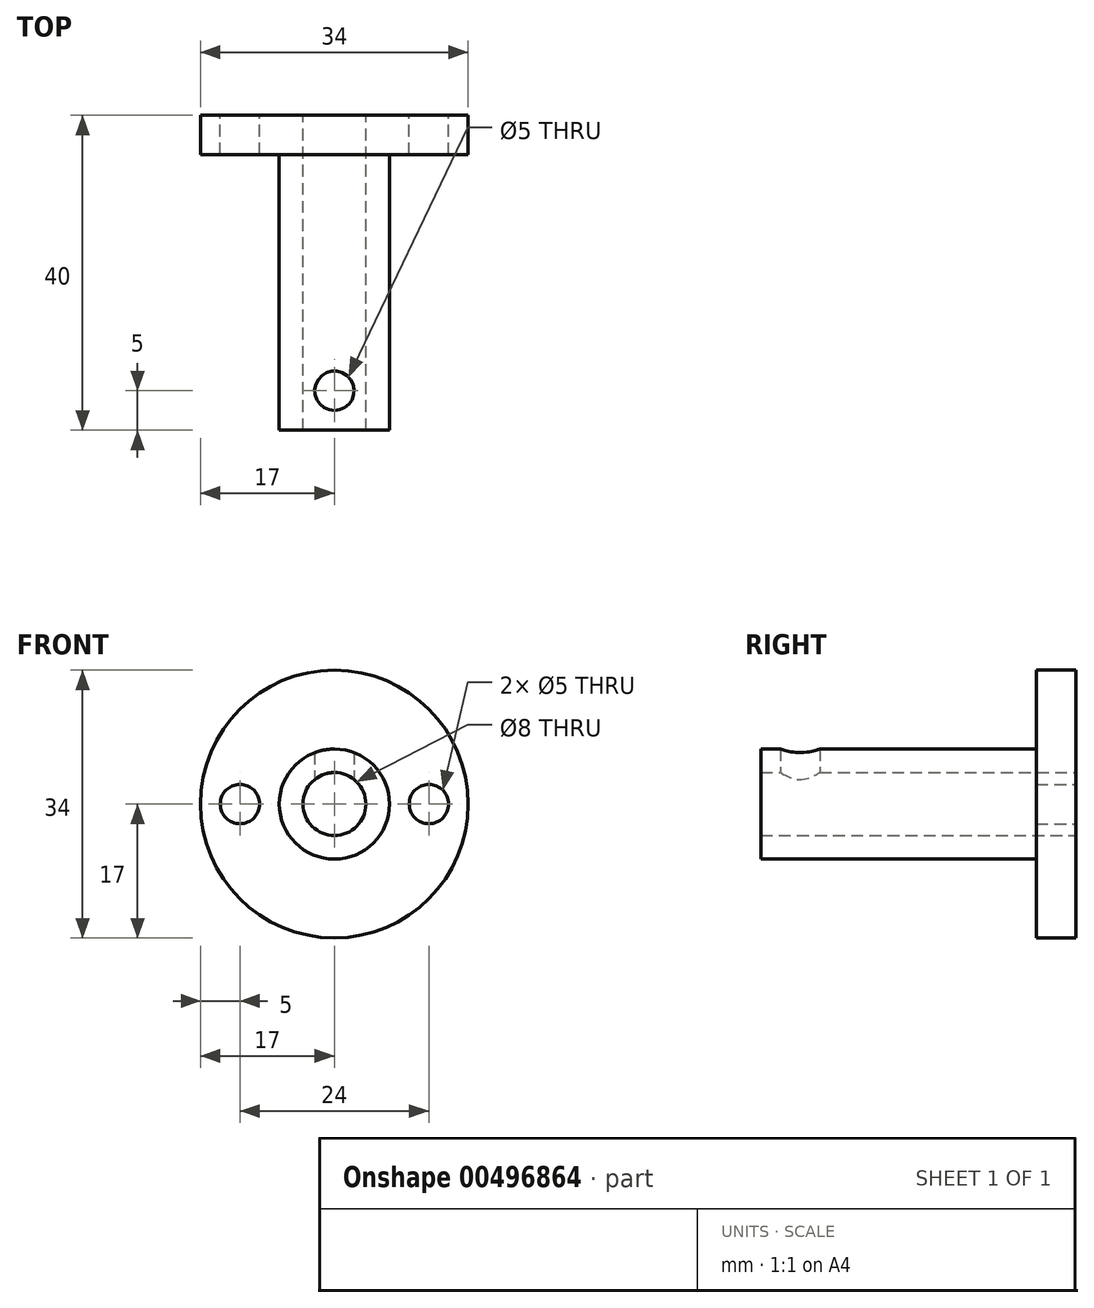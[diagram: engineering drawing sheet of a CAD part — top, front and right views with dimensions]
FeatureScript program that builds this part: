
annotation { "Feature Type Name" : "Feature", "Feature Type Description" : "" }
export const myFeature = defineFeature(function(context is Context, id is Id, definition is map)
    precondition{}
    {
        {
            var Q0;
            Q0=qCreatedBy(makeId("Front.planeOp"),FACE);
            var sketch = newSketch(context, id + "F0", { "sketchPlane" : qUnion([Q0])});
            skCircle(sketch, "E0", {"center": v(0, 0) * mm, "radius": 4 * mm});
            skCircle(sketch, "E1", {"center": v(0, 0) * mm, "radius": 7 * mm});
            skCircle(sketch, "E2", {"center": v(0, 0) * mm, "radius": 17 * mm});
            skCircle(sketch, "E3", {"center": v(-12, 0) * mm, "radius": 2.5 * mm});
            skCircle(sketch, "E4", {"center": v(12, 0) * mm, "radius": 2.5 * mm});
            skSolve(sketch);
        }
        {
            var Q0;
            Q0=makeQuery(id+"F0.imprint","IMPRINT",FACE,{"disambiguationData":[TD([[makeQuery(id+"F0.imprint","IMPRINT",EDGE,{"derivedFrom":sQuery(id+"F0.wireOp",EDGE,"E2")}),1.0]])]});
            extrude(context, id + "F1", {"entities" : qUnion([Q0]), "depth" : 5 * mm});
        }
        {
            var Q0;
            Q0=makeQuery(id+"F0.imprint","IMPRINT",FACE,{"disambiguationData":[TD([[makeQuery(id+"F0.imprint","IMPRINT",EDGE,{"derivedFrom":sQuery(id+"F0.wireOp",EDGE,"E0")}),-1.0]])]});
            extrude(context, id + "F2", {"entities" : qUnion([Q0]), "operationType" : NewBodyOperationType.ADD, "depth" : 40 * mm});
        }
        {
            var Q0;
            Q0=qCreatedBy(makeId("Top.planeOp"),FACE);
            var sketch = newSketch(context, id + "F3", { "sketchPlane" : qUnion([Q0])});
            skLineSegment(sketch, "E5", {"start": v(0, 0) * mm, "end": v(0, -35) * mm});
            skCircle(sketch, "E6", {"center": v(0, -35) * mm, "radius": 2.5 * mm});
            skSolve(sketch);
        }
        {
            var Q0;
            Q0 = qSketchRegion(id + "F3", true);
            extrude(context, id + "F4", {"entities" : qUnion([Q0]), "operationType" : NewBodyOperationType.REMOVE, "depth" : 10 * mm});
        }
    });
